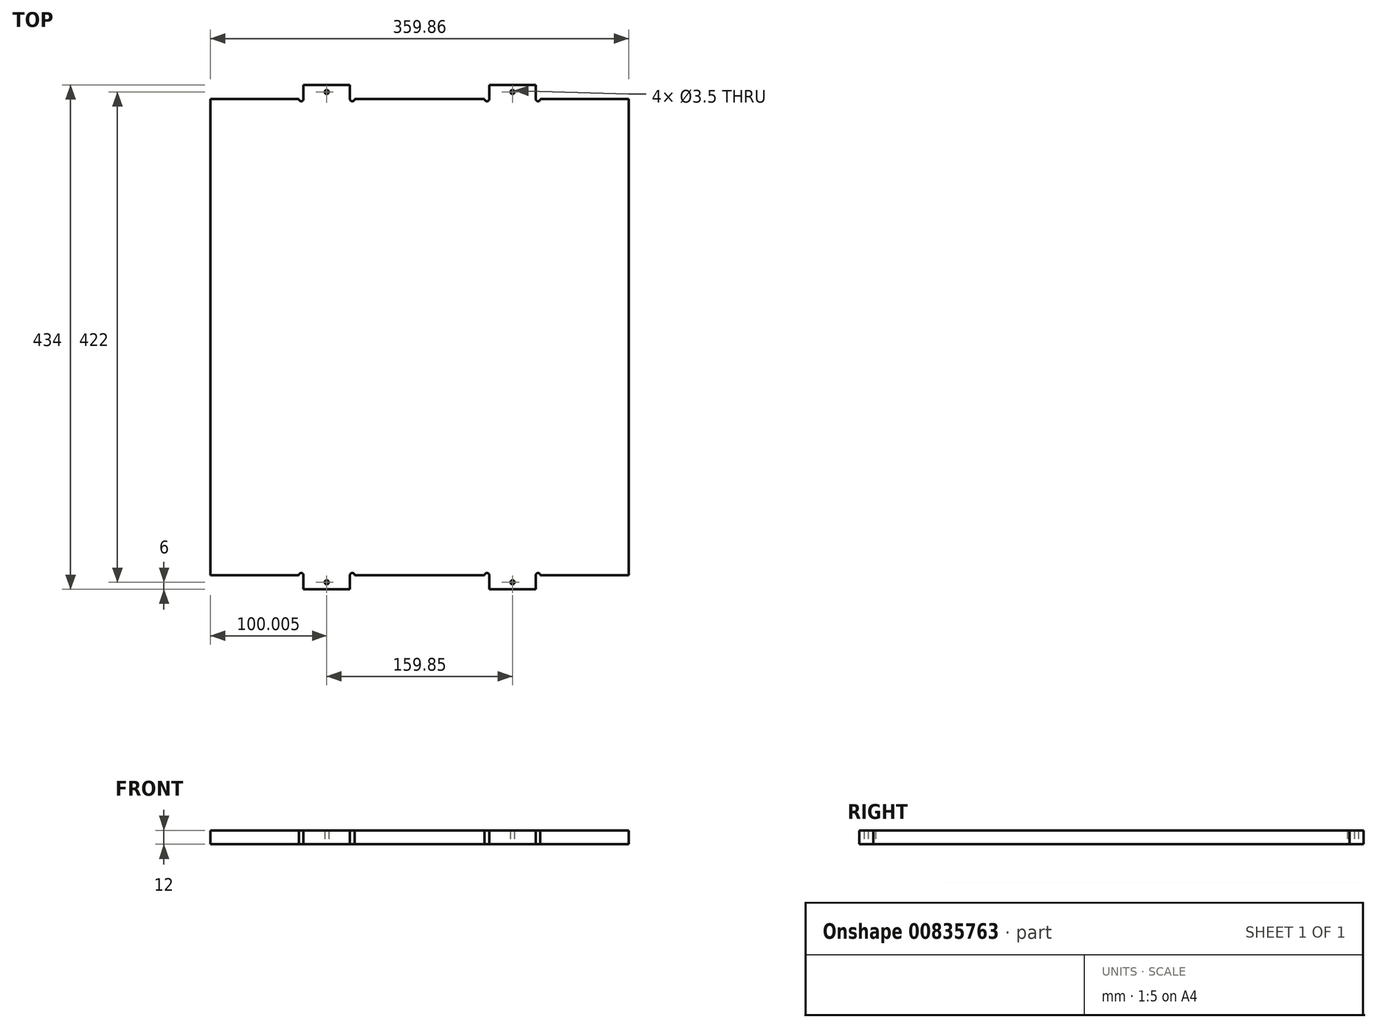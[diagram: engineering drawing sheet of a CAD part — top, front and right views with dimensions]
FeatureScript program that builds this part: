
annotation { "Feature Type Name" : "Feature", "Feature Type Description" : "" }
export const myFeature = defineFeature(function(context is Context, id is Id, definition is map)
    precondition{}
    {
        {
            var Q0;
            Q0=qCreatedBy(makeId("Top.planeOp"),FACE);
            var sketch = newSketch(context, id + "F0", { "sketchPlane" : qUnion([Q0])});
            skLineSegment(sketch, "E0", {"start": v(-179.93, 0) * mm, "end": v(-179.93, 205) * mm});
            skLineSegment(sketch, "E1", {"start": v(-179.93, 205) * mm, "end": v(-103.92, 205) * mm});
            skLineSegment(sketch, "E2", {"start": v(0, 205) * mm, "end": v(0, 0) * mm, "construction": true});
            skLineSegment(sketch, "E3", {"start": v(0, 0) * mm, "end": v(-179.93, 0) * mm, "construction": true});
            skLineSegment(sketch, "E4.top", {"start": v(-99.92, 217) * mm, "end": v(-59.92, 217) * mm});
            skLineSegment(sketch, "E4.left", {"start": v(-99.92, 205) * mm, "end": v(-99.92, 217) * mm});
            skLineSegment(sketch, "E4.right", {"start": v(-59.93, 205) * mm, "end": v(-59.93, 217) * mm});
            skLineSegment(sketch, "E5.trimOffspring", {"start": v(-55.92, 205) * mm, "end": v(0, 205) * mm});
            skArc(sketch, "E6", {"start": v(-99.92, 205) * mm, "mid": v(-101.92, 203) * mm, "end": v(-103.92, 205) * mm});
            skArc(sketch, "E7", {"start": v(-59.92, 205) * mm, "mid": v(-57.92, 203) * mm, "end": v(-55.92, 205) * mm});
            skLineSegment(sketch, "E8.MirrorCS", {"start": v(55.92, 205) * mm, "end": v(0, 205) * mm});
            skLineSegment(sketch, "E9.MirrorCS", {"start": v(59.93, 205) * mm, "end": v(59.93, 217) * mm});
            skLineSegment(sketch, "E10.MirrorCS", {"start": v(99.92, 217) * mm, "end": v(59.92, 217) * mm});
            skLineSegment(sketch, "E11.MirrorCS", {"start": v(99.92, 205) * mm, "end": v(99.92, 217) * mm});
            skLineSegment(sketch, "E12.MirrorCS", {"start": v(179.93, 205) * mm, "end": v(103.92, 205) * mm});
            skLineSegment(sketch, "E13.MirrorCS", {"start": v(179.93, 0) * mm, "end": v(179.93, 205) * mm});
            skArc(sketch, "E14.MirrorCS", {"start": v(59.92, 205) * mm, "mid": v(57.92, 203) * mm, "end": v(55.92, 205) * mm});
            skArc(sketch, "E15.MirrorCS", {"start": v(99.92, 205) * mm, "mid": v(101.92, 203) * mm, "end": v(103.92, 205) * mm});
            skLineSegment(sketch, "E16.MirrorCS", {"start": v(-179.93, 0) * mm, "end": v(-179.93, -205) * mm});
            skLineSegment(sketch, "E17.MirrorCS", {"start": v(-179.93, -205) * mm, "end": v(-103.92, -205) * mm});
            skArc(sketch, "E18.MirrorCS", {"start": v(-99.92, -205) * mm, "mid": v(-101.92, -203) * mm, "end": v(-103.92, -205) * mm});
            skLineSegment(sketch, "E19.MirrorCS", {"start": v(-99.92, -205) * mm, "end": v(-99.92, -217) * mm});
            skLineSegment(sketch, "E20.MirrorCS", {"start": v(-99.92, -217) * mm, "end": v(-59.92, -217) * mm});
            skLineSegment(sketch, "E21.MirrorCS", {"start": v(-59.93, -205) * mm, "end": v(-59.93, -217) * mm});
            skArc(sketch, "E22.MirrorCS", {"start": v(-59.92, -205) * mm, "mid": v(-57.92, -203) * mm, "end": v(-55.92, -205) * mm});
            skLineSegment(sketch, "E23.MirrorCS", {"start": v(-55.92, -205) * mm, "end": v(0, -205) * mm});
            skLineSegment(sketch, "E24.MirrorCS", {"start": v(55.92, -205) * mm, "end": v(0, -205) * mm});
            skArc(sketch, "E25.MirrorCS", {"start": v(59.92, -205) * mm, "mid": v(57.92, -203) * mm, "end": v(55.92, -205) * mm});
            skLineSegment(sketch, "E26.MirrorCS", {"start": v(59.93, -205) * mm, "end": v(59.93, -217) * mm});
            skLineSegment(sketch, "E27.MirrorCS", {"start": v(99.92, -217) * mm, "end": v(59.92, -217) * mm});
            skLineSegment(sketch, "E28.MirrorCS", {"start": v(99.92, -205) * mm, "end": v(99.92, -217) * mm});
            skArc(sketch, "E29.MirrorCS", {"start": v(99.92, -205) * mm, "mid": v(101.92, -203) * mm, "end": v(103.92, -205) * mm});
            skLineSegment(sketch, "E30.MirrorCS", {"start": v(179.93, -205) * mm, "end": v(103.92, -205) * mm});
            skLineSegment(sketch, "E31.MirrorCS", {"start": v(179.93, 0) * mm, "end": v(179.93, -205) * mm});
            skLineSegment(sketch, "E32", {"start": v(-99.92, 211) * mm, "end": v(-59.93, 211) * mm, "construction": true});
            skCircle(sketch, "E33", {"center": v(-79.93, 211) * mm, "radius": 1.75 * mm});
            skCircle(sketch, "E34.MirrorC", {"center": v(79.93, 211) * mm, "radius": 1.75 * mm});
            skCircle(sketch, "E35.MirrorC", {"center": v(-79.93, -211) * mm, "radius": 1.75 * mm});
            skCircle(sketch, "E36.MirrorC", {"center": v(79.93, -211) * mm, "radius": 1.75 * mm});
            skSolve(sketch);
        }
        {
            var Q0;
            Q0=makeQuery(id+"F0.imprint","IMPRINT",FACE,{"disambiguationData":[TD([[makeQuery(id+"F0.imprint","IMPRINT",EDGE,{"derivedFrom":sQuery(id+"F0.wireOp",EDGE,"E0")}),-1.0]])]});
            extrude(context, id + "F1", {"entities" : qUnion([Q0]), "depth" : 12 * mm, "offsetDistance" : 25 * mm});
        }
    });
